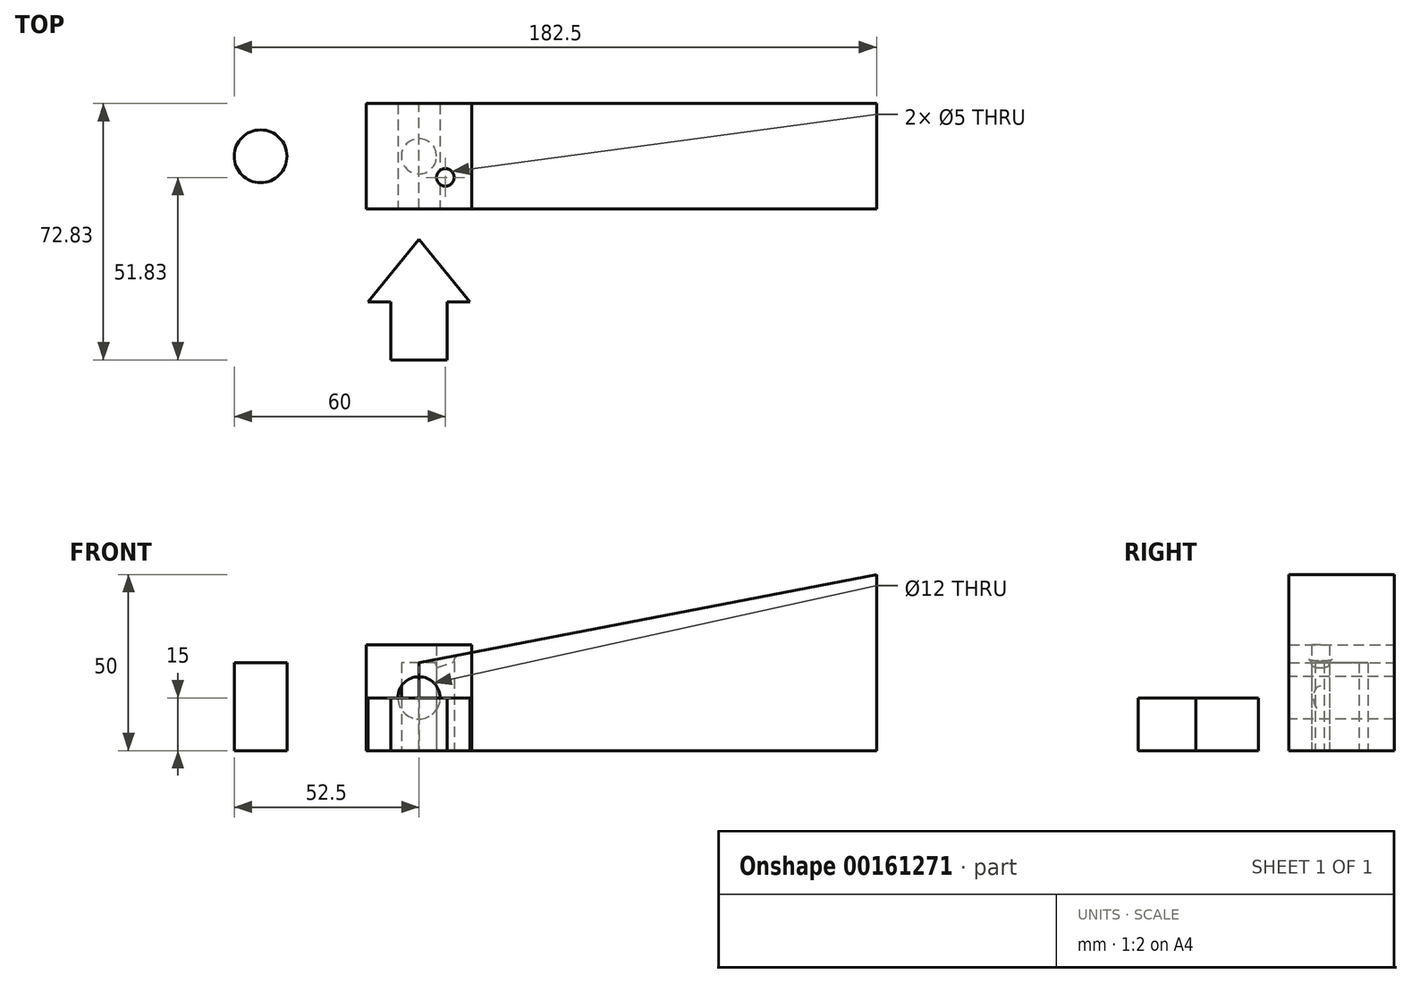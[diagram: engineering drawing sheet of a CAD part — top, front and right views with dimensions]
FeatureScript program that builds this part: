
annotation { "Feature Type Name" : "Feature", "Feature Type Description" : "" }
export const myFeature = defineFeature(function(context is Context, id is Id, definition is map)
    precondition{}
    {
        {
            var Q0;
            Q0=qCreatedBy(makeId("Top.planeOp"),FACE);
            var sketch = newSketch(context, id + "F0", { "sketchPlane" : qUnion([Q0])});
            skLineSegment(sketch, "E0.bottom", {"start": v(15, -15) * mm, "end": v(-15, -15) * mm});
            skLineSegment(sketch, "E0.top", {"start": v(15, 15) * mm, "end": v(-15, 15) * mm});
            skLineSegment(sketch, "E0.left", {"start": v(15, -15) * mm, "end": v(15, 15) * mm});
            skLineSegment(sketch, "E0.right", {"start": v(-15, -15) * mm, "end": v(-15, 15) * mm});
            skPoint(sketch, "E0.middle", {"position": v(0, 0) * mm});
            skSolve(sketch);
        }
        {
            var Q0;
            Q0=makeQuery(id+"F0.imprint","IMPRINT",FACE,{"disambiguationData":[TD([[makeQuery(id+"F0.imprint","IMPRINT",EDGE,{"derivedFrom":sQuery(id+"F0.wireOp",EDGE,"E0.bottom")}),-1.0]])]});
            extrude(context, id + "F1", {"entities" : qUnion([Q0]), "depth" : 30 * mm});
        }
        {
            var Q0;
            Q0=makeQuery(id+"F1.opExtrude","SWEPT_FACE",FACE,{"disambiguationData":[OSD([sQuery(id+"F0.wireOp",EDGE,"E0.bottom")])]});
            var sketch = newSketch(context, id + "F2", { "sketchPlane" : qUnion([Q0])});
            skCircle(sketch, "E1", {"center": v(0, 15) * mm, "radius": 6 * mm});
            skPoint(sketch, "E1.centerSnap0", {"position": v(15, 15) * mm});
            skSolve(sketch);
        }
        {
            var Q0;
            Q0=makeQuery(id+"F2.imprint","IMPRINT",FACE,{"disambiguationData":[TD([[makeQuery(id+"F2.imprint","IMPRINT",EDGE,{"derivedFrom":sQuery(id+"F2.wireOp",EDGE,"E1")}),1.0]])]});
            extrude(context, id + "F3", {"entities" : qUnion([Q0]), "operationType" : NewBodyOperationType.REMOVE, "endBound" : BoundingType.THROUGH_ALL, "oppositeDirection" : true, "depth" : 25 * mm});
        }
        {
            var Q0;
            Q0=qCreatedBy(makeId("Front.planeOp"),FACE);
            var sketch = newSketch(context, id + "F4", { "sketchPlane" : qUnion([Q0])});
            skLineSegment(sketch, "E2", {"start": v(0, 0) * mm, "end": v(0, 25) * mm});
            skLineSegment(sketch, "E3", {"start": v(0, 25) * mm, "end": v(130, 50) * mm});
            skLineSegment(sketch, "E4", {"start": v(130, 50) * mm, "end": v(130, 0) * mm});
            skLineSegment(sketch, "E5", {"start": v(130, 0) * mm, "end": v(0, 0) * mm});
            skSolve(sketch);
        }
        {
            var Q0;
            Q0=makeQuery(id+"F4.imprint","IMPRINT",FACE,{"disambiguationData":[TD([[makeQuery(id+"F4.imprint","IMPRINT",EDGE,{"derivedFrom":sQuery(id+"F4.wireOp",EDGE,"E2")}),-1.0]])]});
            extrude(context, id + "F5", {"entities" : qUnion([Q0]), "endBound" : BoundingType.SYMMETRIC, "depth" : 30 * mm});
        }
        {
            var Q0;
            Q0=makeQuery(id+"F5.opExtrude","SWEPT_FACE",FACE,{"disambiguationData":[OSD([sQuery(id+"F4.wireOp",EDGE,"E5")])]});
            var sketch = newSketch(context, id + "F6", { "sketchPlane" : qUnion([Q0])});
            skCircle(sketch, "E6", {"center": v(7.5, 6) * mm, "radius": 2.5 * mm});
            skSolve(sketch);
        }
        {
            var Q0;
            Q0=makeQuery(id+"F6.imprint","IMPRINT",FACE,{"disambiguationData":[TD([[makeQuery(id+"F6.imprint","IMPRINT",EDGE,{"derivedFrom":sQuery(id+"F6.wireOp",EDGE,"E6")}),1.0]])]});
            extrude(context, id + "F7", {"entities" : qUnion([Q0]), "operationType" : NewBodyOperationType.REMOVE, "endBound" : BoundingType.THROUGH_ALL, "oppositeDirection" : true, "depth" : 25 * mm});
        }
        {
            var Q0;
            Q0=makeQuery(id+"F7.boolean.opBoolean","INTERSECT",EDGE,{"derivedFrom":[makeQuery(id+"F5.opExtrude","SWEPT_FACE",FACE,{"disambiguationData":[OSD([sQuery(id+"F4.wireOp",EDGE,"E3")])]}),makeQuery(id+"F7.opExtrude","SWEPT_FACE",FACE,{"disambiguationData":[OSD([sQuery(id+"F6.wireOp",EDGE,"E6")])]})]});
            fillet(context, id + "F8", {"entities" : qUnion([Q0]), "radius" : 2 * mm, "tangentPropagation" : true, "allowEdgeOverflow" : false});
        }
        {
            var Q0;
            Q0=qCreatedBy(makeId("Top.planeOp"),FACE);
            var sketch = newSketch(context, id + "F9", { "sketchPlane" : qUnion([Q0])});
            skCircle(sketch, "E7", {"center": v(0, 0) * mm, "radius": 5 * mm});
            skCircle(sketch, "E8", {"center": v(-45, 0) * mm, "radius": 7.5 * mm});
            skSolve(sketch);
        }
        {
            var Q0;
            Q0=makeQuery(id+"F9.imprint","IMPRINT",FACE,{"disambiguationData":[TD([[makeQuery(id+"F9.imprint","IMPRINT",EDGE,{"derivedFrom":sQuery(id+"F9.wireOp",EDGE,"E8")}),1.0]])]});
            extrude(context, id + "F10", {"entities" : qUnion([Q0]), "depth" : 25 * mm});
        }
        {
            var Q0;
            Q0=makeQuery(id+"F9.imprint","IMPRINT",FACE,{"disambiguationData":[TD([[makeQuery(id+"F9.imprint","IMPRINT",EDGE,{"derivedFrom":sQuery(id+"F9.wireOp",EDGE,"E7")}),1.0]])]});
            extrude(context, id + "F11", {"entities" : qUnion([Q0]), "depth" : 25 * mm});
        }
        {
            var Q0;
            Q0=qCreatedBy(makeId("Top.planeOp"),FACE);
            var sketch = newSketch(context, id + "F12", { "sketchPlane" : qUnion([Q0])});
            skLineSegment(sketch, "E9", {"start": v(0, 56.45) * mm, "end": v(0, -57.83) * mm, "construction": true});
            skLineSegment(sketch, "E10", {"start": v(0, -57.83) * mm, "end": v(-8, -57.83) * mm});
            skLineSegment(sketch, "E11", {"start": v(-8, -57.83) * mm, "end": v(-8, -41.42) * mm});
            skLineSegment(sketch, "E12", {"start": v(-8, -41.42) * mm, "end": v(-14.53, -41.42) * mm});
            skLineSegment(sketch, "E13", {"start": v(-14.53, -41.42) * mm, "end": v(0, -23.63) * mm});
            skLineSegment(sketch, "E14.MirrorCS", {"start": v(14.53, -41.42) * mm, "end": v(0, -23.63) * mm});
            skLineSegment(sketch, "E15.MirrorCS", {"start": v(8, -41.42) * mm, "end": v(14.53, -41.42) * mm});
            skLineSegment(sketch, "E16.MirrorCS", {"start": v(8, -57.83) * mm, "end": v(8, -41.42) * mm});
            skLineSegment(sketch, "E17.MirrorCS", {"start": v(0, -57.83) * mm, "end": v(8, -57.83) * mm});
            skSolve(sketch);
        }
        {
            var Q0;
            Q0=makeQuery(id+"F12.imprint","IMPRINT",FACE,{"disambiguationData":[TD([[makeQuery(id+"F12.imprint","IMPRINT",EDGE,{"derivedFrom":sQuery(id+"F12.wireOp",EDGE,"E10")}),-1.0]])]});
            extrude(context, id + "F13", {"entities" : qUnion([Q0]), "depth" : 15 * mm});
        }
    });
